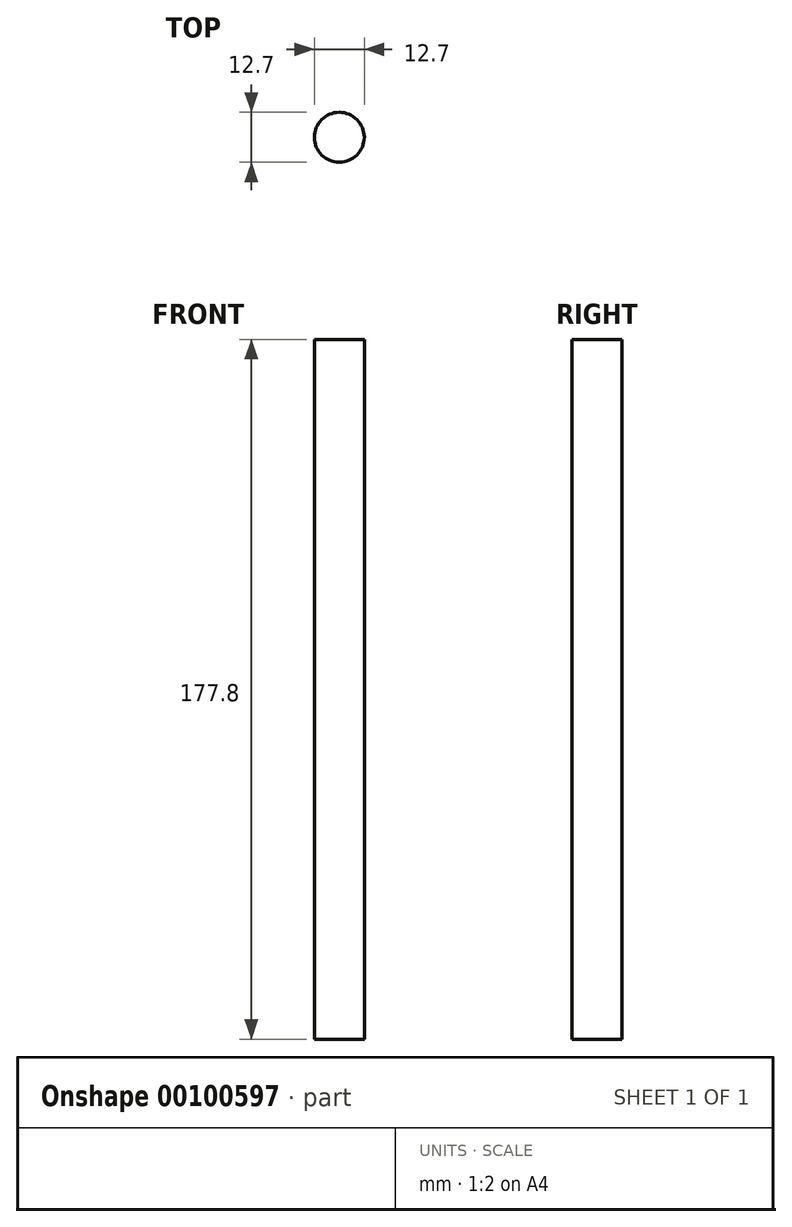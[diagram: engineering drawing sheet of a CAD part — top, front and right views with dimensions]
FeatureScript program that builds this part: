
annotation { "Feature Type Name" : "Feature", "Feature Type Description" : "" }
export const myFeature = defineFeature(function(context is Context, id is Id, definition is map)
    precondition{}
    {
        {
            var Q0;
            Q0=qCreatedBy(makeId("Top.planeOp"),FACE);
            var sketch = newSketch(context, id + "F0", { "sketchPlane" : qUnion([Q0])});
            skCircle(sketch, "E0", {"center": v(0, 0) * mm, "radius": 6.35 * mm});
            skSolve(sketch);
        }
        {
            var Q0;
            Q0 = qSketchRegion(id + "F0", true);
            extrude(context, id + "F1", {"entities" : qUnion([Q0]), "depth" : 177.8 * mm});
        }
    });
